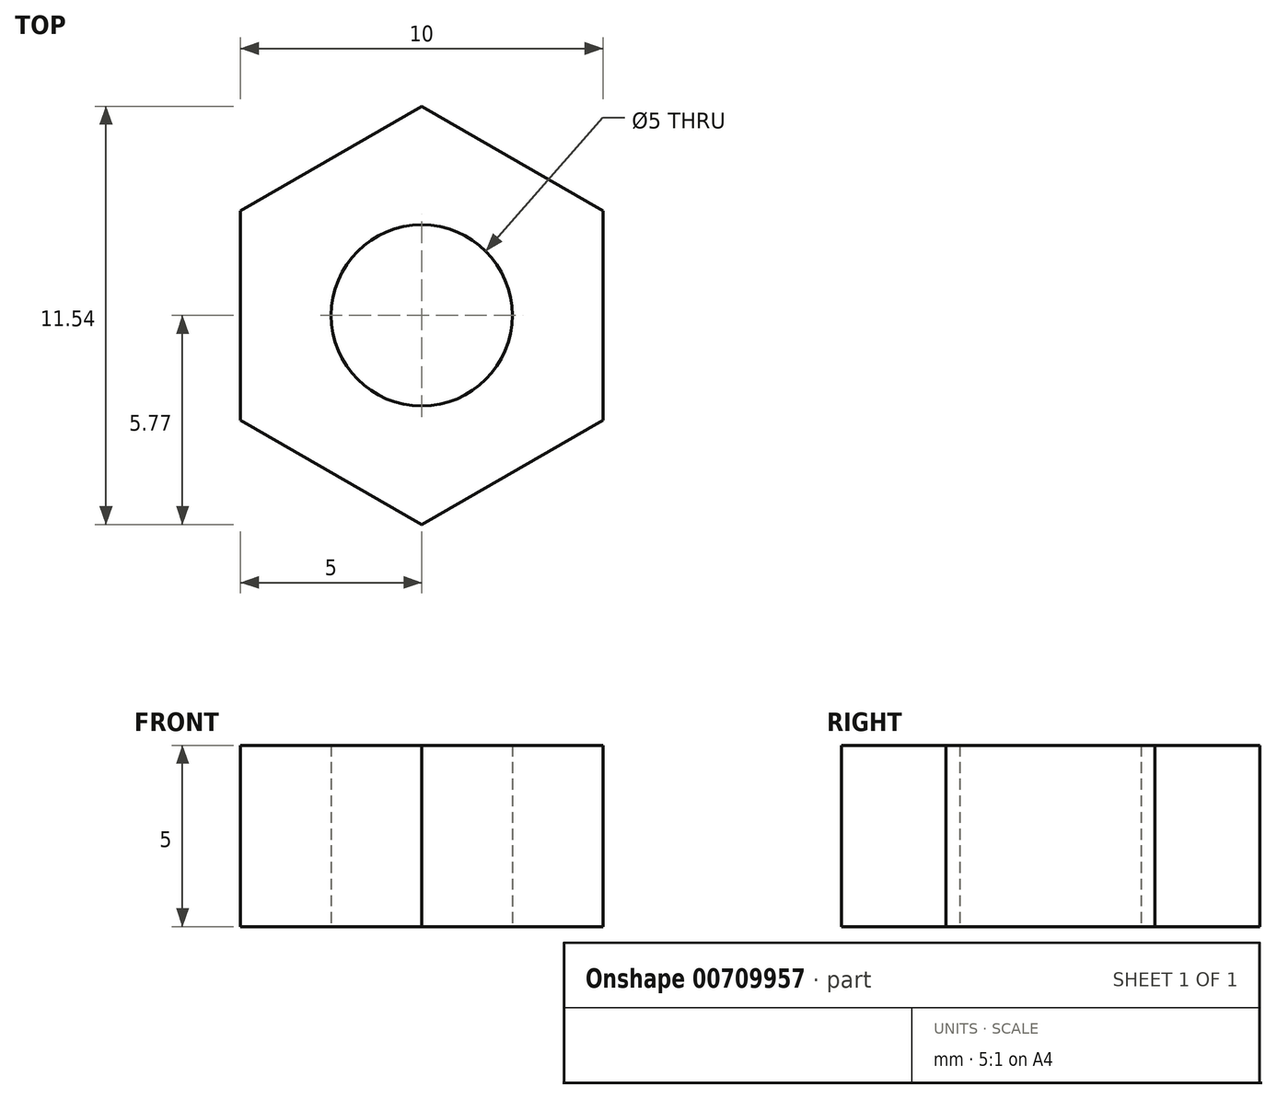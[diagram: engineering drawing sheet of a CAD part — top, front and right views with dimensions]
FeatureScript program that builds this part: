
annotation { "Feature Type Name" : "Feature", "Feature Type Description" : "" }
export const myFeature = defineFeature(function(context is Context, id is Id, definition is map)
    precondition{}
    {
        {
            var Q0;
            Q0=qCreatedBy(makeId("Top.planeOp"),FACE);
            var sketch = newSketch(context, id + "F0", { "sketchPlane" : qUnion([Q0])});
            skCircle(sketch, "E0.cCircle", {"center": v(0, 0) * mm, "radius": 5 * mm, "construction": true});
            skLineSegment(sketch, "E0.0", {"start": v(5, 2.89) * mm, "end": v(5, -2.89) * mm});
            skLineSegment(sketch, "E0.1", {"start": v(5, -2.89) * mm, "end": v(0, -5.77) * mm});
            skLineSegment(sketch, "E0.2", {"start": v(0, -5.77) * mm, "end": v(-5, -2.89) * mm});
            skLineSegment(sketch, "E0.3", {"start": v(-5, -2.89) * mm, "end": v(-5, 2.89) * mm});
            skLineSegment(sketch, "E0.4", {"start": v(-5, 2.89) * mm, "end": v(0, 5.77) * mm});
            skLineSegment(sketch, "E0.5", {"start": v(0, 5.77) * mm, "end": v(5, 2.89) * mm});
            skPoint(sketch, "E0.0.midPoint", {"position": v(5, 0) * mm});
            skCircle(sketch, "E1", {"center": v(0, 0) * mm, "radius": 2.5 * mm});
            skSolve(sketch);
        }
        {
            var Q0;
            Q0=makeQuery(id+"F0.imprint","IMPRINT",FACE,{"disambiguationData":[TD([[makeQuery(id+"F0.imprint","IMPRINT",EDGE,{"derivedFrom":sQuery(id+"F0.wireOp",EDGE,"E0.0")}),-1.0]])]});
            extrude(context, id + "F1", {"entities" : qUnion([Q0]), "depth" : 5 * mm, "offsetDistance" : 25 * mm});
        }
    });
